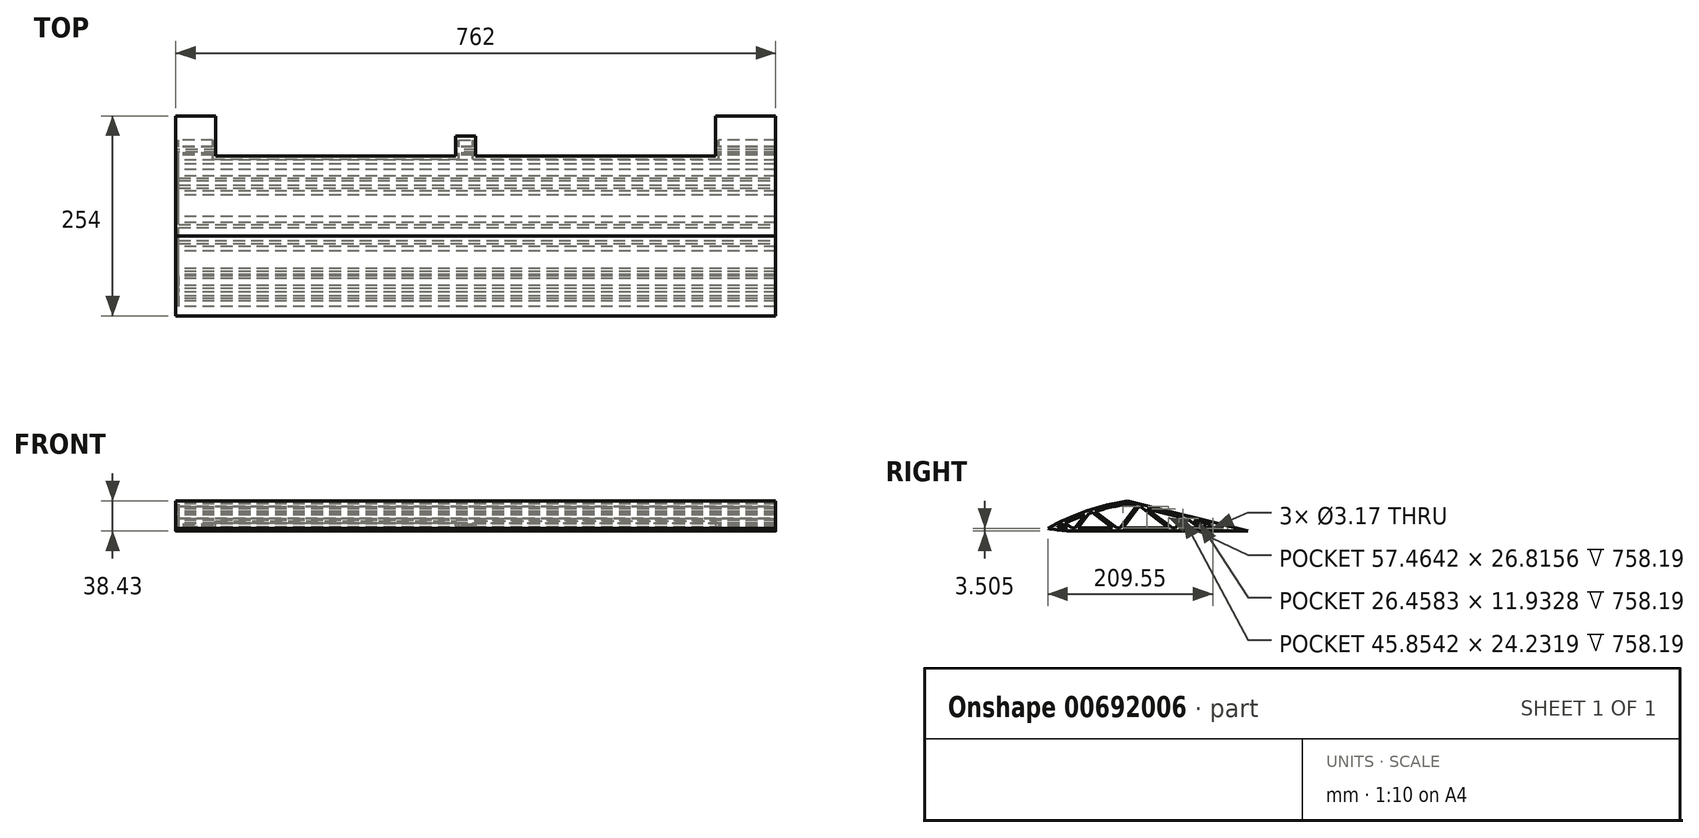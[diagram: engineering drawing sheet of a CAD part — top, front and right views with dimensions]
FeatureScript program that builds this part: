
annotation { "Feature Type Name" : "Feature", "Feature Type Description" : "" }
export const myFeature = defineFeature(function(context is Context, id is Id, definition is map)
    precondition{}
    {
        {
            var Q0;
            Q0=qCreatedBy(makeId("Right.planeOp"),FACE);
            var sketch = newSketch(context, id + "F0", { "sketchPlane" : qUnion([Q0])});
            skLineSegment(sketch, "E0.bottom", {"start": v(-127, 19.05) * mm, "end": v(127, 19.05) * mm});
            skLineSegment(sketch, "E0.top", {"start": v(-127, -19.05) * mm, "end": v(-120.65, -19.05) * mm});
            skLineSegment(sketch, "E0.left", {"start": v(-127, 19.05) * mm, "end": v(-127, -19.05) * mm});
            skLineSegment(sketch, "E0.right", {"start": v(127, 19.05) * mm, "end": v(127, -19.05) * mm});
            skPoint(sketch, "E0.middle", {"position": v(0, 0) * mm});
            skLineSegment(sketch, "E1", {"start": v(-123.83, -17.46) * mm, "end": v(-127, -15.88) * mm});
            skLineSegment(sketch, "E2", {"start": v(-127, 19.05) * mm, "end": v(-76.2, 19.05) * mm});
            skLineSegment(sketch, "E3", {"start": v(-76.2, 19.05) * mm, "end": v(-76.2, 6.35) * mm});
            skLineSegment(sketch, "E4", {"start": v(-127, 19.05) * mm, "end": v(-25.4, 19.05) * mm});
            skLineSegment(sketch, "E5", {"start": v(-25.4, 19.05) * mm, "end": v(127, -19.05) * mm});
            skLineSegment(sketch, "E6", {"start": v(-76.2, 6.35) * mm, "end": v(-76.2, -19.05) * mm});
            skArc(sketch, "E7", {"start": v(-127, -15.88) * mm, "mid": v(-101.7, -18.95) * mm, "end": v(-76.2, -19.05) * mm});
            skLineSegment(sketch, "E8.trimOffspring", {"start": v(-76.2, -19.05) * mm, "end": v(127, -19.05) * mm});
            skPoint(sketch, "E9.orphan", {"position": v(-123.83, -17.46) * mm});
            skPoint(sketch, "E10.orphan", {"position": v(-76.2, -17.46) * mm});
            skPoint(sketch, "E11.end.orphan", {"position": v(-100.01, -17.46) * mm});
            skArc(sketch, "E12", {"start": v(-25.4, 19.05) * mm, "mid": v(-77.67, 5.85) * mm, "end": v(-127, -15.88) * mm});
            skLineSegment(sketch, "E13", {"start": v(127, -19.05) * mm, "end": v(101.6, -19.05) * mm});
            skLineSegment(sketch, "E14", {"start": v(101.6, -19.05) * mm, "end": v(76.2, -19.05) * mm});
            skLineSegment(sketch, "E15", {"start": v(76.2, -19.05) * mm, "end": v(50.8, 0) * mm});
            skLineSegment(sketch, "E16", {"start": v(50.8, 0) * mm, "end": v(36.51, -19.05) * mm});
            skLineSegment(sketch, "E17", {"start": v(36.51, -19.05) * mm, "end": v(-8.73, 14.88) * mm});
            skLineSegment(sketch, "E18", {"start": v(-8.73, 14.88) * mm, "end": v(-34.18, -19.05) * mm});
            skLineSegment(sketch, "E19", {"start": v(-34.18, -19.05) * mm, "end": v(-70.53, 8.21) * mm});
            skLineSegment(sketch, "E20", {"start": v(-70.53, 8.21) * mm, "end": v(-91.2, -19.35) * mm});
            skLineSegment(sketch, "E21", {"start": v(-91.2, -19.35) * mm, "end": v(-108.35, -6.5) * mm});
            skLineSegment(sketch, "E22", {"start": v(76.2, -19.05) * mm, "end": v(74.3, -21.6) * mm});
            skLineSegment(sketch, "E23", {"start": v(74.3, -21.6) * mm, "end": v(48.9, -2.54) * mm});
            skLineSegment(sketch, "E24", {"start": v(48.9, -2.54) * mm, "end": v(46.36, -0.64) * mm});
            skLineSegment(sketch, "E25", {"start": v(46.36, -0.64) * mm, "end": v(33.97, -17.14) * mm});
            skLineSegment(sketch, "E26", {"start": v(33.97, -17.14) * mm, "end": v(32.07, -19.68) * mm});
            skLineSegment(sketch, "E27", {"start": v(32.07, -19.68) * mm, "end": v(-10.64, 12.34) * mm});
            skLineSegment(sketch, "E28", {"start": v(-10.64, 12.34) * mm, "end": v(-13.18, 14.25) * mm});
            skLineSegment(sketch, "E29", {"start": v(-13.18, 14.25) * mm, "end": v(-36.72, -17.14) * mm});
            skLineSegment(sketch, "E30", {"start": v(-36.72, -17.14) * mm, "end": v(-38.63, -19.68) * mm});
            skLineSegment(sketch, "E31", {"start": v(-38.63, -19.68) * mm, "end": v(-72.43, 5.67) * mm});
            skLineSegment(sketch, "E32", {"start": v(-72.43, 5.67) * mm, "end": v(-74.97, 7.58) * mm});
            skLineSegment(sketch, "E33", {"start": v(-74.97, 7.58) * mm, "end": v(-93.74, -17.45) * mm});
            skLineSegment(sketch, "E34", {"start": v(-93.74, -17.45) * mm, "end": v(-95.65, -19.99) * mm});
            skLineSegment(sketch, "E35", {"start": v(-95.65, -19.99) * mm, "end": v(-111.6, -8.02) * mm});
            skLineSegment(sketch, "E36", {"start": v(127, -19.05) * mm, "end": v(82.55, -19.05) * mm});
            skLineSegment(sketch, "E37", {"start": v(82.55, -19.05) * mm, "end": v(82.55, -15.88) * mm});
            skCircle(sketch, "E38", {"center": v(82.55, -15.88) * mm, "radius": 1.59 * mm});
            skSolve(sketch);
        }
        {
            var Q0;
            {var subQ0=sQuery(id+"F0.wireOp",EDGE,"E1");Q0=makeQuery(id+"F0.imprint","IMPRINT",FACE,{"disambiguationData":[TD([[makeQuery(id+"F0.imprint","IMPRINT",EDGE,{"derivedFrom":subQ0}),-1.0]])]});}
            var Q1;
            {var subQ0=sQuery(id+"F0.wireOp",EDGE,"E5");Q1=makeQuery(id+"F0.imprint","IMPRINT",FACE,{"disambiguationData":[TD([[makeQuery(id+"F0.imprint","IMPRINT",EDGE,{"derivedFrom":subQ0}),-1.0]])]});}
            var Q2;
            {var subQ0=sQuery(id+"F0.wireOp",EDGE,"E15");Q2=makeQuery(id+"F0.imprint","IMPRINT",FACE,{"disambiguationData":[TD([[makeQuery(id+"F0.imprint","IMPRINT",EDGE,{"derivedFrom":subQ0}),1.0]])]});}
            var Q3;
            {var subQ0=sQuery(id+"F0.wireOp",EDGE,"E23");var subQ1=sQuery(id+"F0.wireOp",EDGE,"E8.trimOffspring");var subQ2=makeQuery(id+"F0.imprint","INTERSECT",VERTEX,{"derivedFrom":[subQ1,subQ0]});Q3=makeQuery(id+"F0.imprint","IMPRINT",FACE,{"disambiguationData":[TD([[makeQuery(id+"F0.imprint","IMPRINT",EDGE,{"disambiguationData":[TD([[subQ2,1.0]])],"derivedFrom":subQ1}),1.0]])]});}
            var Q4;
            {var subQ0=sQuery(id+"F0.wireOp",EDGE,"E24");Q4=makeQuery(id+"F0.imprint","IMPRINT",FACE,{"disambiguationData":[TD([[makeQuery(id+"F0.imprint","IMPRINT",EDGE,{"derivedFrom":subQ0}),1.0]])]});}
            var Q5;
            {var subQ4=sQuery(id+"F0.wireOp",EDGE,"E24");Q5=makeQuery(id+"F0.imprint","IMPRINT",FACE,{"disambiguationData":[TD([[makeQuery(id+"F0.imprint","IMPRINT",EDGE,{"derivedFrom":subQ4}),-1.0]])]});}
            var Q6;
            {var subQ1=sQuery(id+"F0.wireOp",EDGE,"E8.trimOffspring");var subQ3=sQuery(id+"F0.wireOp",EDGE,"E27");var subQ4=makeQuery(id+"F0.imprint","INTERSECT",VERTEX,{"derivedFrom":[subQ1,subQ3]});Q6=makeQuery(id+"F0.imprint","IMPRINT",FACE,{"disambiguationData":[TD([[makeQuery(id+"F0.imprint","IMPRINT",EDGE,{"disambiguationData":[TD([[subQ4,1.0]])],"derivedFrom":subQ1}),1.0]])]});}
            var Q7;
            {var subQ8=sQuery(id+"F0.wireOp",EDGE,"E28");Q7=makeQuery(id+"F0.imprint","IMPRINT",FACE,{"disambiguationData":[TD([[makeQuery(id+"F0.imprint","IMPRINT",EDGE,{"derivedFrom":subQ8}),-1.0]])]});}
            var Q8;
            {var subQ0=sQuery(id+"F0.wireOp",EDGE,"E20");var subQ1=sQuery(id+"F0.wireOp",EDGE,"E6");var subQ2=makeQuery(id+"F0.imprint","INTERSECT",VERTEX,{"derivedFrom":[subQ1,subQ0]});Q8=makeQuery(id+"F0.imprint","IMPRINT",FACE,{"disambiguationData":[TD([[makeQuery(id+"F0.imprint","IMPRINT",EDGE,{"disambiguationData":[TD([[subQ2,-1.0]])],"derivedFrom":subQ1}),1.0]])]});}
            var Q9;
            {var subQ1=sQuery(id+"F0.wireOp",EDGE,"E6");var subQ3=sQuery(id+"F0.wireOp",EDGE,"E33");var subQ4=makeQuery(id+"F0.imprint","INTERSECT",VERTEX,{"derivedFrom":[subQ1,subQ3]});Q9=makeQuery(id+"F0.imprint","IMPRINT",FACE,{"disambiguationData":[TD([[makeQuery(id+"F0.imprint","IMPRINT",EDGE,{"disambiguationData":[TD([[subQ4,1.0]])],"derivedFrom":subQ1}),-1.0]])]});}
            var Q10;
            {var subQ3=sQuery(id+"F0.wireOp",EDGE,"E7");var subQ7=sQuery(id+"F0.wireOp",EDGE,"E35");var subQ9=makeQuery(id+"F0.imprint","INTERSECT",VERTEX,{"derivedFrom":[subQ3,subQ7]});Q10=makeQuery(id+"F0.imprint","IMPRINT",FACE,{"disambiguationData":[TD([[makeQuery(id+"F0.imprint","IMPRINT",EDGE,{"disambiguationData":[TD([[subQ9,-1.0]])],"derivedFrom":subQ3}),1.0]])]});}
            var Q11;
            {var subQ0=sQuery(id+"F0.wireOp",EDGE,"E20");var subQ1=sQuery(id+"F0.wireOp",EDGE,"E6");var subQ2=makeQuery(id+"F0.imprint","INTERSECT",VERTEX,{"derivedFrom":[subQ1,subQ0]});Q11=makeQuery(id+"F0.imprint","IMPRINT",FACE,{"disambiguationData":[TD([[makeQuery(id+"F0.imprint","IMPRINT",EDGE,{"disambiguationData":[TD([[subQ2,1.0]])],"derivedFrom":subQ1}),-1.0]])]});}
            var Q12;
            {var subQ0=sQuery(id+"F0.wireOp",EDGE,"E30");var subQ1=sQuery(id+"F0.wireOp",EDGE,"E8.trimOffspring");var subQ2=makeQuery(id+"F0.imprint","INTERSECT",VERTEX,{"derivedFrom":[subQ1,subQ0]});Q12=makeQuery(id+"F0.imprint","IMPRINT",FACE,{"disambiguationData":[TD([[makeQuery(id+"F0.imprint","IMPRINT",EDGE,{"disambiguationData":[TD([[subQ2,1.0]])],"derivedFrom":subQ1}),1.0]])]});}
            var Q13;
            {var subQ1=sQuery(id+"F0.wireOp",EDGE,"E20");var subQ5=sQuery(id+"F0.wireOp",EDGE,"E6");var subQ6=makeQuery(id+"F0.imprint","INTERSECT",VERTEX,{"derivedFrom":[subQ5,subQ1]});Q13=makeQuery(id+"F0.imprint","IMPRINT",FACE,{"disambiguationData":[TD([[makeQuery(id+"F0.imprint","IMPRINT",EDGE,{"disambiguationData":[TD([[subQ6,1.0]])],"derivedFrom":subQ5}),1.0]])]});}
            var Q14;
            {var subQ3=sQuery(id+"F0.wireOp",EDGE,"E28");Q14=makeQuery(id+"F0.imprint","IMPRINT",FACE,{"disambiguationData":[TD([[makeQuery(id+"F0.imprint","IMPRINT",EDGE,{"derivedFrom":subQ3}),1.0]])]});}
            var Q15;
            {var subQ3=sQuery(id+"F0.wireOp",EDGE,"E8.trimOffspring");var subQ7=sQuery(id+"F0.wireOp",EDGE,"E27");var subQ9=makeQuery(id+"F0.imprint","INTERSECT",VERTEX,{"derivedFrom":[subQ3,subQ7]});Q15=makeQuery(id+"F0.imprint","IMPRINT",FACE,{"disambiguationData":[TD([[makeQuery(id+"F0.imprint","IMPRINT",EDGE,{"disambiguationData":[TD([[subQ9,-1.0]])],"derivedFrom":subQ3}),1.0]])]});}
            var Q16;
            {var subQ1=sQuery(id+"F0.wireOp",EDGE,"E8.trimOffspring");var subQ3=sQuery(id+"F0.wireOp",EDGE,"E26");var subQ4=makeQuery(id+"F0.imprint","INTERSECT",VERTEX,{"derivedFrom":[subQ1,subQ3]});Q16=makeQuery(id+"F0.imprint","IMPRINT",FACE,{"disambiguationData":[TD([[makeQuery(id+"F0.imprint","IMPRINT",EDGE,{"disambiguationData":[TD([[subQ4,-1.0]])],"derivedFrom":subQ1}),1.0]])]});}
            var Q17;
            {var subQ1=sQuery(id+"F0.wireOp",EDGE,"E8.trimOffspring");var subQ3=sQuery(id+"F0.wireOp",EDGE,"E30");var subQ4=makeQuery(id+"F0.imprint","INTERSECT",VERTEX,{"derivedFrom":[subQ1,subQ3]});Q17=makeQuery(id+"F0.imprint","IMPRINT",FACE,{"disambiguationData":[TD([[makeQuery(id+"F0.imprint","IMPRINT",EDGE,{"disambiguationData":[TD([[subQ4,-1.0]])],"derivedFrom":subQ1}),1.0]])]});}
            var Q18;
            {var subQ0=sQuery(id+"F0.wireOp",EDGE,"E34");var subQ1=sQuery(id+"F0.wireOp",EDGE,"E7");var subQ2=makeQuery(id+"F0.imprint","INTERSECT",VERTEX,{"derivedFrom":[subQ1,subQ0]});Q18=makeQuery(id+"F0.imprint","IMPRINT",FACE,{"disambiguationData":[TD([[makeQuery(id+"F0.imprint","IMPRINT",EDGE,{"disambiguationData":[TD([[subQ2,-1.0]])],"derivedFrom":subQ1}),1.0]])]});}
            var Q19;
            {var subQ0=sQuery(id+"F0.wireOp",EDGE,"E20");var subQ1=sQuery(id+"F0.wireOp",EDGE,"E6");var subQ2=makeQuery(id+"F0.imprint","INTERSECT",VERTEX,{"derivedFrom":[subQ1,subQ0]});Q19=makeQuery(id+"F0.imprint","IMPRINT",FACE,{"disambiguationData":[TD([[makeQuery(id+"F0.imprint","IMPRINT",EDGE,{"disambiguationData":[TD([[subQ2,-1.0]])],"derivedFrom":subQ1}),-1.0]])]});}
            var Q20;
            {var subQ1=sQuery(id+"F0.wireOp",EDGE,"E12");var subQ3=sQuery(id+"F0.wireOp",EDGE,"E32");var subQ4=makeQuery(id+"F0.imprint","INTERSECT",VERTEX,{"derivedFrom":[subQ1,subQ3]});Q20=makeQuery(id+"F0.imprint","IMPRINT",FACE,{"disambiguationData":[TD([[makeQuery(id+"F0.imprint","IMPRINT",EDGE,{"disambiguationData":[TD([[subQ4,1.0]])],"derivedFrom":subQ1}),1.0]])]});}
            var Q21;
            {var subQ1=sQuery(id+"F0.wireOp",EDGE,"E6");var subQ3=sQuery(id+"F0.wireOp",EDGE,"E33");var subQ4=makeQuery(id+"F0.imprint","INTERSECT",VERTEX,{"derivedFrom":[subQ1,subQ3]});Q21=makeQuery(id+"F0.imprint","IMPRINT",FACE,{"disambiguationData":[TD([[makeQuery(id+"F0.imprint","IMPRINT",EDGE,{"disambiguationData":[TD([[subQ4,1.0]])],"derivedFrom":subQ3}),-1.0]])]});}
            var Q22;
            {var subQ1=sQuery(id+"F0.wireOp",EDGE,"E7");var subQ3=sQuery(id+"F0.wireOp",EDGE,"E35");var subQ4=makeQuery(id+"F0.imprint","INTERSECT",VERTEX,{"derivedFrom":[subQ1,subQ3]});Q22=makeQuery(id+"F0.imprint","IMPRINT",FACE,{"disambiguationData":[TD([[makeQuery(id+"F0.imprint","IMPRINT",EDGE,{"disambiguationData":[TD([[subQ4,-1.0]])],"derivedFrom":subQ3}),1.0]])]});}
            extrude(context, id + "F1", {"entities" : qUnion([Q0, Q1, Q2, Q3, Q4, Q5, Q6, Q7, Q8, Q9, Q10, Q11, Q12, Q13, Q14, Q15, Q16, Q17, Q18, Q19, Q20, Q21, Q22]), "depth" : 762 * mm, "offsetDistance" : 25.4 * mm});
        }
        {
            var Q0;
            Q0=makeQuery(id+"F1.opExtrude","SWEPT_BODY",BODY,{"disambiguationData":[OSD([sQuery(id+"F0.wireOp",EDGE,"E0.top"),sQuery(id+"F0.wireOp",EDGE,"E1"),sQuery(id+"F0.wireOp",EDGE,"54O46Pbj-JXbp-sWDO-WlFE-3hnwlmeF4VM1"),sQuery(id+"F0.wireOp",EDGE,"I7tgXKDc-7YU1-26Oo-DtxB-X4BbDVzCFCnU"),sQuery(id+"F0.wireOp",EDGE,"E5")])]});
            var Q1;
            Q1=qCreatedBy(makeId("Right.planeOp"),FACE);
            mirror(context, id + "F2", {"operationType" : NewBodyOperationType.ADD, "entities" : qUnion([Q0]), "mirrorPlane" : qUnion([Q1])});
        }
        {
            var Q0;
            {var subQ0=sQuery(id+"F0.wireOp",EDGE,"E15");Q0=makeQuery(id+"F0.imprint","IMPRINT",FACE,{"disambiguationData":[TD([[makeQuery(id+"F0.imprint","IMPRINT",EDGE,{"derivedFrom":subQ0}),1.0]])]});}
            var Q1;
            {var subQ0=sQuery(id+"F0.wireOp",EDGE,"E24");Q1=makeQuery(id+"F0.imprint","IMPRINT",FACE,{"disambiguationData":[TD([[makeQuery(id+"F0.imprint","IMPRINT",EDGE,{"derivedFrom":subQ0}),1.0]])]});}
            var Q2;
            {var subQ3=sQuery(id+"F0.wireOp",EDGE,"E8.trimOffspring");var subQ7=sQuery(id+"F0.wireOp",EDGE,"E27");var subQ9=makeQuery(id+"F0.imprint","INTERSECT",VERTEX,{"derivedFrom":[subQ3,subQ7]});Q2=makeQuery(id+"F0.imprint","IMPRINT",FACE,{"disambiguationData":[TD([[makeQuery(id+"F0.imprint","IMPRINT",EDGE,{"disambiguationData":[TD([[subQ9,-1.0]])],"derivedFrom":subQ3}),1.0]])]});}
            var Q3;
            {var subQ3=sQuery(id+"F0.wireOp",EDGE,"E28");Q3=makeQuery(id+"F0.imprint","IMPRINT",FACE,{"disambiguationData":[TD([[makeQuery(id+"F0.imprint","IMPRINT",EDGE,{"derivedFrom":subQ3}),1.0]])]});}
            var Q4;
            {var subQ0=sQuery(id+"F0.wireOp",EDGE,"E30");var subQ1=sQuery(id+"F0.wireOp",EDGE,"E8.trimOffspring");var subQ2=makeQuery(id+"F0.imprint","INTERSECT",VERTEX,{"derivedFrom":[subQ1,subQ0]});Q4=makeQuery(id+"F0.imprint","IMPRINT",FACE,{"disambiguationData":[TD([[makeQuery(id+"F0.imprint","IMPRINT",EDGE,{"disambiguationData":[TD([[subQ2,1.0]])],"derivedFrom":subQ1}),1.0]])]});}
            var Q5;
            {var subQ0=sQuery(id+"F0.wireOp",EDGE,"E20");var subQ1=sQuery(id+"F0.wireOp",EDGE,"E6");var subQ2=makeQuery(id+"F0.imprint","INTERSECT",VERTEX,{"derivedFrom":[subQ1,subQ0]});Q5=makeQuery(id+"F0.imprint","IMPRINT",FACE,{"disambiguationData":[TD([[makeQuery(id+"F0.imprint","IMPRINT",EDGE,{"disambiguationData":[TD([[subQ2,1.0]])],"derivedFrom":subQ1}),-1.0]])]});}
            var Q6;
            {var subQ3=sQuery(id+"F0.wireOp",EDGE,"E7");var subQ7=sQuery(id+"F0.wireOp",EDGE,"E35");var subQ9=makeQuery(id+"F0.imprint","INTERSECT",VERTEX,{"derivedFrom":[subQ3,subQ7]});Q6=makeQuery(id+"F0.imprint","IMPRINT",FACE,{"disambiguationData":[TD([[makeQuery(id+"F0.imprint","IMPRINT",EDGE,{"disambiguationData":[TD([[subQ9,-1.0]])],"derivedFrom":subQ3}),1.0]])]});}
            var Q7;
            {var subQ1=sQuery(id+"F0.wireOp",EDGE,"E20");var subQ5=sQuery(id+"F0.wireOp",EDGE,"E6");var subQ6=makeQuery(id+"F0.imprint","INTERSECT",VERTEX,{"derivedFrom":[subQ5,subQ1]});Q7=makeQuery(id+"F0.imprint","IMPRINT",FACE,{"disambiguationData":[TD([[makeQuery(id+"F0.imprint","IMPRINT",EDGE,{"disambiguationData":[TD([[subQ6,1.0]])],"derivedFrom":subQ5}),1.0]])]});}
            extrude(context, id + "F3", {"entities" : qUnion([Q0, Q1, Q2, Q3, Q4, Q5, Q6, Q7]), "operationType" : NewBodyOperationType.ADD, "depth" : 762 * mm, "offsetDistance" : 25.4 * mm});
        }
        {
            var Q0;
            {var subQ0=makeQuery(id+"F1.opExtrude","SWEPT_FACE",FACE,{"disambiguationData":[OSD([sQuery(id+"F0.wireOp",EDGE,"E8.trimOffspring")])]});Q0=makeQuery(id+"F2.boolean.opBoolean","MERGE",FACE,{"derivedFrom":[subQ0,makeQuery(id+"F2.opPattern","COPY",FACE,{"derivedFrom":subQ0,"instanceName":"1"})]});}
            var sketch = newSketch(context, id + "F4", { "sketchPlane" : qUnion([Q0])});
            skLineSegment(sketch, "E39", {"start": v(0, -127) * mm, "end": v(0, 312.49) * mm});
            skLineSegment(sketch, "E40", {"start": v(0, 312.49) * mm, "end": v(931.06, 312.49) * mm});
            skLineSegment(sketch, "E41", {"start": v(931.06, 312.49) * mm, "end": v(931.06, -488.96) * mm});
            skLineSegment(sketch, "E42", {"start": v(931.06, -488.96) * mm, "end": v(0, -488.96) * mm});
            skLineSegment(sketch, "E43", {"start": v(0, -488.96) * mm, "end": v(0, 0) * mm});
            skSolve(sketch);
        }
        {
            var Q0;
            {var subQ0=sQuery(id+"F0.wireOp",EDGE,"E8.trimOffspring");var subQ1=makeQuery(id+"F1.opExtrude","CAP_EDGE",EDGE,{"disambiguationData":[OSD([subQ0])],"isStart":false});var subQ2=makeQuery(id+"F4.imprint","IMPRINT",EDGE,{"derivedFrom":subQ1});var subQ14=sQuery(id+"F4.wireOp",EDGE,"E40");Q0=qUnion([makeQuery(id+"F4.imprint","IMPRINT",FACE,{"disambiguationData":[TD([[makeQuery(id+"F4.imprint","IMPRINT",EDGE,{"derivedFrom":subQ14}),-1.0]])]}),makeQuery(id+"F4.imprint","IMPRINT",FACE,{"disambiguationData":[TD([[subQ2,-1.0]])]})]);}
            extrude(context, id + "F5", {"entities" : qUnion([Q0]), "operationType" : NewBodyOperationType.REMOVE, "endBound" : BoundingType.THROUGH_ALL, "oppositeDirection" : true, "depth" : 25.4 * mm, "offsetDistance" : 25.4 * mm});
        }
        {
            var Q0;
            {var subQ0=sQuery(id+"F4.wireOp",EDGE,"E40");Q0=makeQuery(id+"F4.imprint","IMPRINT",FACE,{"disambiguationData":[TD([[makeQuery(id+"F4.imprint","IMPRINT",EDGE,{"derivedFrom":subQ0}),-1.0]])]});}
            extrude(context, id + "F6", {"entities" : qUnion([Q0]), "operationType" : NewBodyOperationType.REMOVE, "endBound" : BoundingType.THROUGH_ALL, "depth" : 25.4 * mm, "offsetDistance" : 25.4 * mm});
        }
        {
            var Q0;
            {var subQ0=sQuery(id+"F0.wireOp",EDGE,"E8.trimOffspring");var subQ3=makeQuery(id+"F2.opPattern","COPY",EDGE,{"derivedFrom":makeQuery(id+"F1.opExtrude","CAP_EDGE",EDGE,{"disambiguationData":[OSD([subQ0])],"isStart":false}),"instanceName":"1"});Q0=makeQuery(id+"F4.imprint","IMPRINT",FACE,{"disambiguationData":[TD([[makeQuery(id+"F4.imprint","IMPRINT",EDGE,{"derivedFrom":subQ3}),1.0]])]});}
            var sketch = newSketch(context, id + "F7", { "sketchPlane" : qUnion([Q0])});
            skLineSegment(sketch, "E44", {"start": v(0, 0) * mm, "end": v(0, -127) * mm});
            skLineSegment(sketch, "E45", {"start": v(0, -127) * mm, "end": v(0, -50.8) * mm});
            skLineSegment(sketch, "E46", {"start": v(0, -50.8) * mm, "end": v(0, -127) * mm});
            skLineSegment(sketch, "E47", {"start": v(0, -127) * mm, "end": v(-76.2, -127) * mm});
            skLineSegment(sketch, "E48", {"start": v(-76.2, -127) * mm, "end": v(-76.2, -76.2) * mm});
            skLineSegment(sketch, "E49", {"start": v(-76.2, -76.2) * mm, "end": v(-711.2, -76.2) * mm});
            skLineSegment(sketch, "E50", {"start": v(-711.2, -76.2) * mm, "end": v(-711.2, -127) * mm});
            skLineSegment(sketch, "E51.bottom", {"start": v(-381, -50.8) * mm, "end": v(-406.4, -50.8) * mm});
            skLineSegment(sketch, "E51.top", {"start": v(-381, -101.6) * mm, "end": v(-406.4, -101.6) * mm});
            skLineSegment(sketch, "E51.left", {"start": v(-381, -50.8) * mm, "end": v(-381, -101.6) * mm});
            skLineSegment(sketch, "E51.right", {"start": v(-406.4, -50.8) * mm, "end": v(-406.4, -101.6) * mm});
            skPoint(sketch, "E51.middle", {"position": v(-393.7, -76.2) * mm});
            skSolve(sketch);
        }
        {
            var Q0;
            {var subQ0=sQuery(id+"F7.wireOp",EDGE,"E48");Q0=makeQuery(id+"F7.imprint","IMPRINT",FACE,{"disambiguationData":[TD([[makeQuery(id+"F7.imprint","IMPRINT",EDGE,{"derivedFrom":subQ0}),1.0]])]});}
            extrude(context, id + "F8", {"entities" : qUnion([Q0]), "operationType" : NewBodyOperationType.REMOVE, "oppositeDirection" : true, "depth" : 25.4 * mm, "offsetDistance" : 25.4 * mm});
        }
        {
            var Q0;
            {var subQ0=sQuery(id+"F4.wireOp",EDGE,"E39");Q0=makeQuery(id+"F6.boolean.opBoolean","MERGE",FACE,{"derivedFrom":[makeQuery(id+"F5.boolean.opBoolean","COPY",FACE,{"derivedFrom":makeQuery(id+"F5.opExtrude","SWEPT_FACE",FACE,{"disambiguationData":[OSD([subQ0,sQuery(id+"F4.wireOp",EDGE,"E43")])]})})],"fromTools":[makeQuery(id+"F6.opExtrude","SWEPT_FACE",FACE,{"disambiguationData":[OSD([subQ0])]})]});}
            shell(context, id + "F9", {"entities" : qUnion([Q0]), "thickness" : 3.8 * mm});
        }
        {
            var Q0;
            {var subQ0=sQuery(id+"F0.wireOp",EDGE,"E20");var subQ1=sQuery(id+"F0.wireOp",EDGE,"E6");var subQ2=makeQuery(id+"F0.imprint","INTERSECT",VERTEX,{"derivedFrom":[subQ1,subQ0]});Q0=makeQuery(id+"F0.imprint","IMPRINT",FACE,{"disambiguationData":[TD([[makeQuery(id+"F0.imprint","IMPRINT",EDGE,{"disambiguationData":[TD([[subQ2,1.0]])],"derivedFrom":subQ1}),-1.0]])]});}
            var Q1;
            {var subQ3=sQuery(id+"F0.wireOp",EDGE,"E7");var subQ7=sQuery(id+"F0.wireOp",EDGE,"E35");var subQ9=makeQuery(id+"F0.imprint","INTERSECT",VERTEX,{"derivedFrom":[subQ3,subQ7]});Q1=makeQuery(id+"F0.imprint","IMPRINT",FACE,{"disambiguationData":[TD([[makeQuery(id+"F0.imprint","IMPRINT",EDGE,{"disambiguationData":[TD([[subQ9,-1.0]])],"derivedFrom":subQ3}),1.0]])]});}
            var Q2;
            {var subQ1=sQuery(id+"F0.wireOp",EDGE,"E20");var subQ5=sQuery(id+"F0.wireOp",EDGE,"E6");var subQ6=makeQuery(id+"F0.imprint","INTERSECT",VERTEX,{"derivedFrom":[subQ5,subQ1]});Q2=makeQuery(id+"F0.imprint","IMPRINT",FACE,{"disambiguationData":[TD([[makeQuery(id+"F0.imprint","IMPRINT",EDGE,{"disambiguationData":[TD([[subQ6,1.0]])],"derivedFrom":subQ5}),1.0]])]});}
            var Q3;
            {var subQ0=sQuery(id+"F0.wireOp",EDGE,"E30");var subQ1=sQuery(id+"F0.wireOp",EDGE,"E8.trimOffspring");var subQ2=makeQuery(id+"F0.imprint","INTERSECT",VERTEX,{"derivedFrom":[subQ1,subQ0]});Q3=makeQuery(id+"F0.imprint","IMPRINT",FACE,{"disambiguationData":[TD([[makeQuery(id+"F0.imprint","IMPRINT",EDGE,{"disambiguationData":[TD([[subQ2,1.0]])],"derivedFrom":subQ1}),1.0]])]});}
            var Q4;
            {var subQ3=sQuery(id+"F0.wireOp",EDGE,"E28");Q4=makeQuery(id+"F0.imprint","IMPRINT",FACE,{"disambiguationData":[TD([[makeQuery(id+"F0.imprint","IMPRINT",EDGE,{"derivedFrom":subQ3}),1.0]])]});}
            var Q5;
            {var subQ3=sQuery(id+"F0.wireOp",EDGE,"E8.trimOffspring");var subQ7=sQuery(id+"F0.wireOp",EDGE,"E27");var subQ9=makeQuery(id+"F0.imprint","INTERSECT",VERTEX,{"derivedFrom":[subQ3,subQ7]});Q5=makeQuery(id+"F0.imprint","IMPRINT",FACE,{"disambiguationData":[TD([[makeQuery(id+"F0.imprint","IMPRINT",EDGE,{"disambiguationData":[TD([[subQ9,-1.0]])],"derivedFrom":subQ3}),1.0]])]});}
            var Q6;
            {var subQ0=sQuery(id+"F0.wireOp",EDGE,"E24");Q6=makeQuery(id+"F0.imprint","IMPRINT",FACE,{"disambiguationData":[TD([[makeQuery(id+"F0.imprint","IMPRINT",EDGE,{"derivedFrom":subQ0}),1.0]])]});}
            var Q7;
            {var subQ0=sQuery(id+"F0.wireOp",EDGE,"E15");Q7=makeQuery(id+"F0.imprint","IMPRINT",FACE,{"disambiguationData":[TD([[makeQuery(id+"F0.imprint","IMPRINT",EDGE,{"derivedFrom":subQ0}),1.0]])]});}
            extrude(context, id + "F10", {"entities" : qUnion([Q0, Q1, Q2, Q3, Q4, Q5, Q6, Q7]), "operationType" : NewBodyOperationType.ADD, "oppositeDirection" : true, "depth" : 762 * mm, "offsetDistance" : 25.4 * mm});
        }
    });
